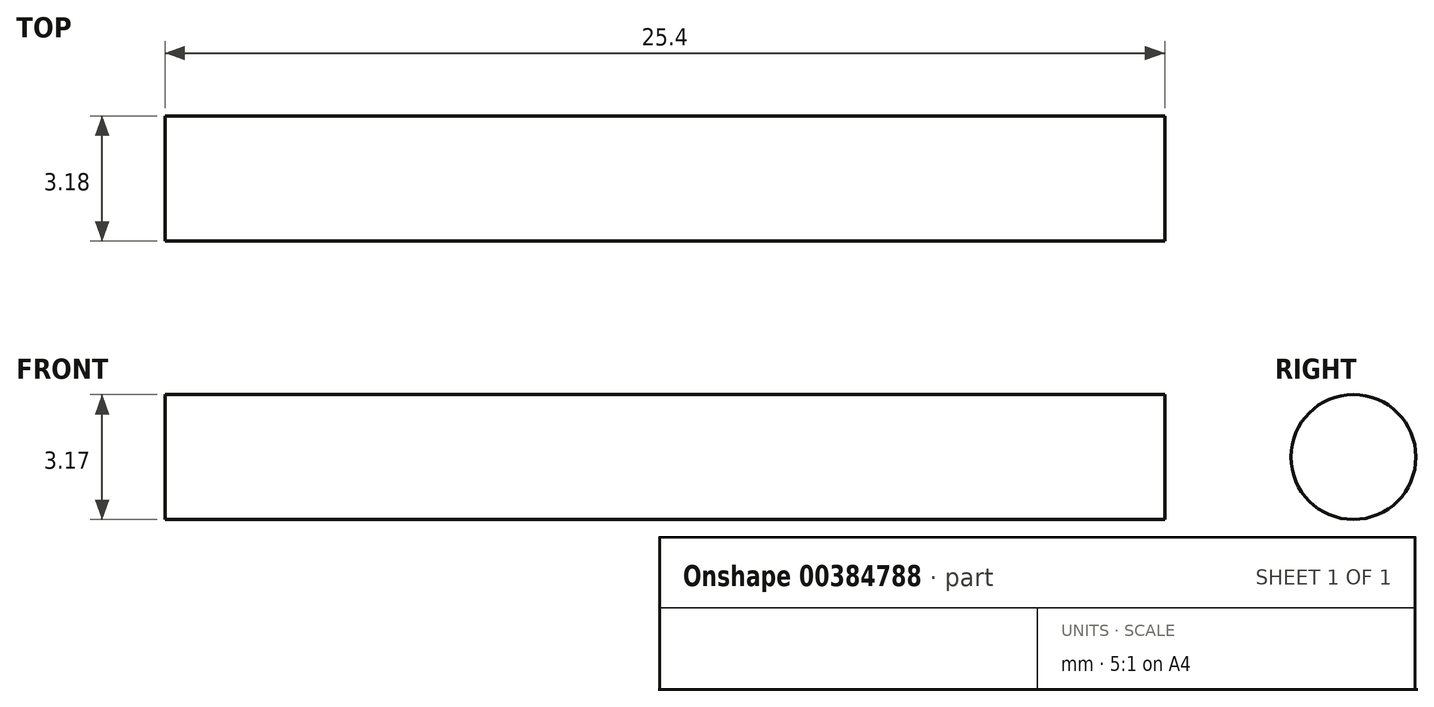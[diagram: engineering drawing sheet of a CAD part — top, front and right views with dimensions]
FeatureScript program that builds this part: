
annotation { "Feature Type Name" : "Feature", "Feature Type Description" : "" }
export const myFeature = defineFeature(function(context is Context, id is Id, definition is map)
    precondition{}
    {
        {
            var Q0;
            Q0=qCreatedBy(makeId("Right.planeOp"),FACE);
            var sketch = newSketch(context, id + "F0", { "sketchPlane" : qUnion([Q0])});
            skCircle(sketch, "E0", {"center": v(-39.3, 31.1) * mm, "radius": 1.59 * mm});
            skSolve(sketch);
        }
        {
            var Q0;
            Q0=makeQuery(id+"F0.imprint","IMPRINT",FACE,{"disambiguationData":[TD([[makeQuery(id+"F0.imprint","IMPRINT",EDGE,{"derivedFrom":sQuery(id+"F0.wireOp",EDGE,"E0")}),1.0]])]});
            extrude(context, id + "F1", {"entities" : qUnion([Q0]), "depth" : 25.4 * mm});
        }
    });
